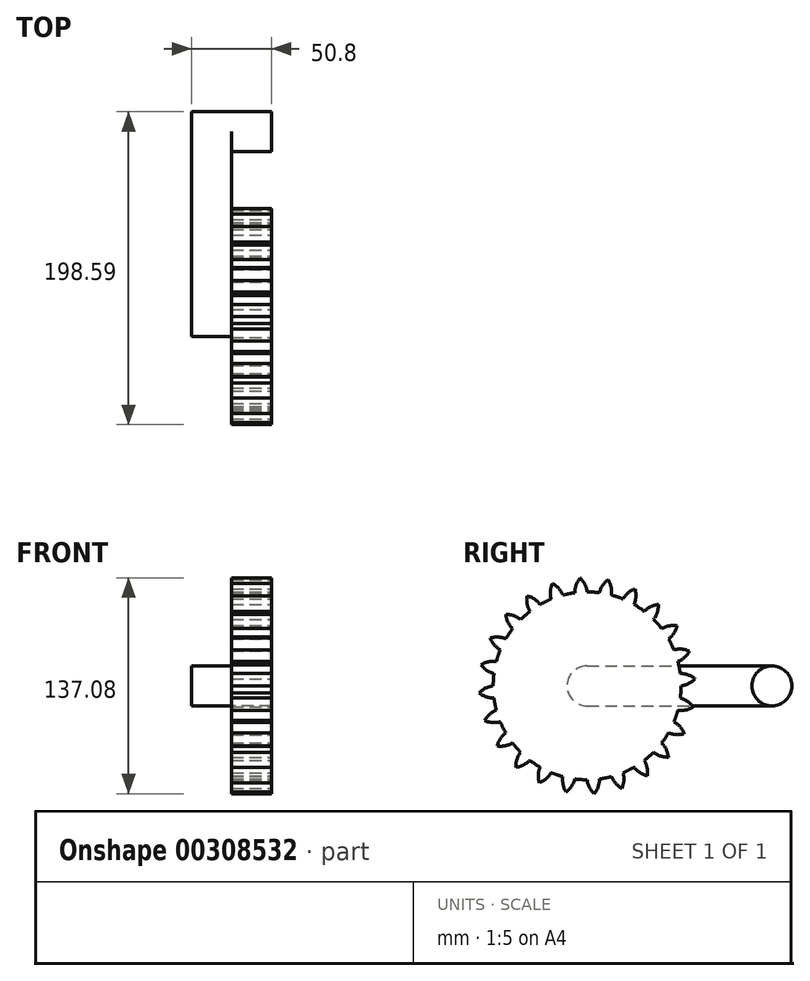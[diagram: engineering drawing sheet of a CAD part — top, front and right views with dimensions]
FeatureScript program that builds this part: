
annotation { "Feature Type Name" : "Feature", "Feature Type Description" : "" }
export const myFeature = defineFeature(function(context is Context, id is Id, definition is map)
    precondition{}
    {
        {
            var Q0;
            Q0=qCreatedBy(makeId("Right.planeOp"),FACE);
            var sketch = newSketch(context, id + "F0", { "sketchPlane" : qUnion([Q0])});
            skLineSegment(sketch, "E0.bottom", {"start": v(0, 0) * mm, "end": v(117.35, 0) * mm});
            skLineSegment(sketch, "E0.top", {"start": v(0, 25.4) * mm, "end": v(117.35, 25.4) * mm});
            skLineSegment(sketch, "E0.left", {"start": v(0, 0) * mm, "end": v(0, 25.4) * mm});
            skLineSegment(sketch, "E0.right", {"start": v(117.35, 0) * mm, "end": v(117.35, 25.4) * mm});
            skCircle(sketch, "E1", {"center": v(0, 12.7) * mm, "radius": 12.7 * mm});
            skCircle(sketch, "E2", {"center": v(117.35, 12.7) * mm, "radius": 12.7 * mm});
            skSolve(sketch);
        }
        {
            var Q0;
            Q0 = qSketchRegion(id + "F0", true);
            extrude(context, id + "F1", {"entities" : qUnion([Q0]), "depth" : 25.4 * mm});
        }
        {
            var Q0;
            {var subQ0=sQuery(id+"F0.wireOp",EDGE,"E0.left");Q0=makeQuery(id+"F0.imprint","IMPRINT",FACE,{"disambiguationData":[TD([[makeQuery(id+"F0.imprint","IMPRINT",EDGE,{"derivedFrom":subQ0}),1.0]])]});}
            var Q1;
            {var subQ0=sQuery(id+"F0.wireOp",EDGE,"E0.left");Q1=makeQuery(id+"F0.imprint","IMPRINT",FACE,{"disambiguationData":[TD([[makeQuery(id+"F0.imprint","IMPRINT",EDGE,{"derivedFrom":subQ0}),-1.0]])]});}
            var Q2;
            {var subQ0=sQuery(id+"F0.wireOp",EDGE,"E0.right");Q2=makeQuery(id+"F0.imprint","IMPRINT",FACE,{"disambiguationData":[TD([[makeQuery(id+"F0.imprint","IMPRINT",EDGE,{"derivedFrom":subQ0}),-1.0]])]});}
            var Q3;
            {var subQ0=sQuery(id+"F0.wireOp",EDGE,"E0.right");Q3=makeQuery(id+"F0.imprint","IMPRINT",FACE,{"disambiguationData":[TD([[makeQuery(id+"F0.imprint","IMPRINT",EDGE,{"derivedFrom":subQ0}),1.0]])]});}
            extrude(context, id + "F2", {"entities" : qUnion([Q0, Q1, Q2, Q3]), "operationType" : NewBodyOperationType.ADD, "depth" : 50.8 * mm});
        }
        {
            var Q0;
            Q0=makeQuery(id+"F2.opExtrude","CAP_FACE",FACE,{"disambiguationData":[OSD([sQuery(id+"F0.wireOp",EDGE,"E1")])],"isStart":false});
            var sketch = newSketch(context, id + "F3", { "sketchPlane" : qUnion([Q0])});
            skCircle(sketch, "E3", {"center": v(0, 12.7) * mm, "radius": 12.7 * mm});
            skCircle(sketch, "E4", {"center": v(0, 12.7) * mm, "radius": 53.72 * mm, "construction": true});
            skCircle(sketch, "E5", {"center": v(0, 12.7) * mm, "radius": 58.67 * mm, "construction": true});
            skCircle(sketch, "E6", {"center": v(0, 12.7) * mm, "radius": 63.5 * mm, "construction": true});
            skLineSegment(sketch, "E7", {"start": v(0, 12.7) * mm, "end": v(0, 97.37) * mm, "construction": true});
            skLineSegment(sketch, "E8", {"start": v(0, 12.7) * mm, "end": v(-6.21, 107.45) * mm, "construction": true});
            skLineSegment(sketch, "E9", {"start": v(0, 76.2) * mm, "end": v(-81.91, 76.2) * mm, "construction": true});
            skLineSegment(sketch, "E10", {"start": v(0, 76.2) * mm, "end": v(-90.62, 43.22) * mm, "construction": true});
            skCircle(sketch, "E11", {"center": v(0, 12.7) * mm, "radius": 59.67 * mm});
            skCircle(sketch, "E12", {"center": v(0, 72.37) * mm, "radius": 14.6 * mm, "construction": true});
            skCircle(sketch, "E13", {"center": v(-14.49, 70.59) * mm, "radius": 14.6 * mm, "construction": true});
            skArc(sketch, "E14", {"start": v(0, 72.37) * mm, "mid": v(-1.46, 77.2) * mm, "end": v(-4.5, 81.24) * mm});
            skArc(sketch, "E15.MirrorCS", {"start": v(-7.78, 71.86) * mm, "mid": v(-6.97, 76.84) * mm, "end": v(-4.5, 81.24) * mm});
            skSolve(sketch);
        }
        {
            var Q0;
            Q0 = qSketchRegion(id + "F3", true);
            extrude(context, id + "F4", {"entities" : qUnion([Q0]), "oppositeDirection" : true, "depth" : 25.4 * mm});
        }
        {
            var Q0;
            Q0=makeQuery(id+"F4.opExtrude","SWEPT_BODY",BODY,{"disambiguationData":[OSD([sQuery(id+"F3.wireOp",EDGE,"E3"),sQuery(id+"F3.wireOp",EDGE,"E11"),sQuery(id+"F3.wireOp",EDGE,"E14"),sQuery(id+"F3.wireOp",EDGE,"E15.MirrorCS")])]});
            var Q1;
            Q1=makeQuery(id+"F4.opExtrude","SWEPT_FACE",FACE,{"disambiguationData":[OSD([sQuery(id+"F3.wireOp",EDGE,"E11")])]});
            circularPattern(context, id + "F5", {"operationType" : NewBodyOperationType.ADD, "entities" : qUnion([Q0]), "axis" : qUnion([Q1]), "angle" : 15 * degree, "instanceCount" : 24});
        }
    });
